# Revit family: Haworth_Cappellini_Gong_Table_EU_PRELIMINARY
name_source: partatom
category: Furniture
revit_build: Autodesk Revit 2018 (Build: 20170223_1515(x64)
units: mm (PartAtom-declared; Revit-internal decimal feet)

## family parameters
Always vertical = Yes
Cut with Voids When Loaded = No
OmniClass Number = 23.40.20.00
OmniClass Title = General Furniture and Specialties
Room Calculation Point = No
Shared = No
Work Plane-Based = No

## types (3) — shared parameters
Assembly Code = E2020200
Description = Haworth - Cappellini - Gong - Table
Manufacturer = Haworth
Model = GG_XX
Radius = 2 cm
Revision = 1
Size = Verify Final Dim. w/ Haworth
URL = https://www.haworth.com
URL - Product = https://www.haworth.com
Warranty = http://www.haworth.com

## per-type parameters (varying)
| type | Actual Diameter | Actual Height | Circus Top | Large | Plain Top | Small | Worksurface Width |
| Small - Plain Top | 50 cm | 42 cm | No | No | Yes | Yes | 25 cm |
| Large - Plain Top | 74 cm | 28 cm | No | Yes | Yes | No | 37 cm |
| Small - Circus Top | 50 cm | 42 cm | Yes | No | No | Yes | 25 cm |

## geometry (parser evidence)
native form markers: Sweep x2
no freeform markers — native parametric forms only
